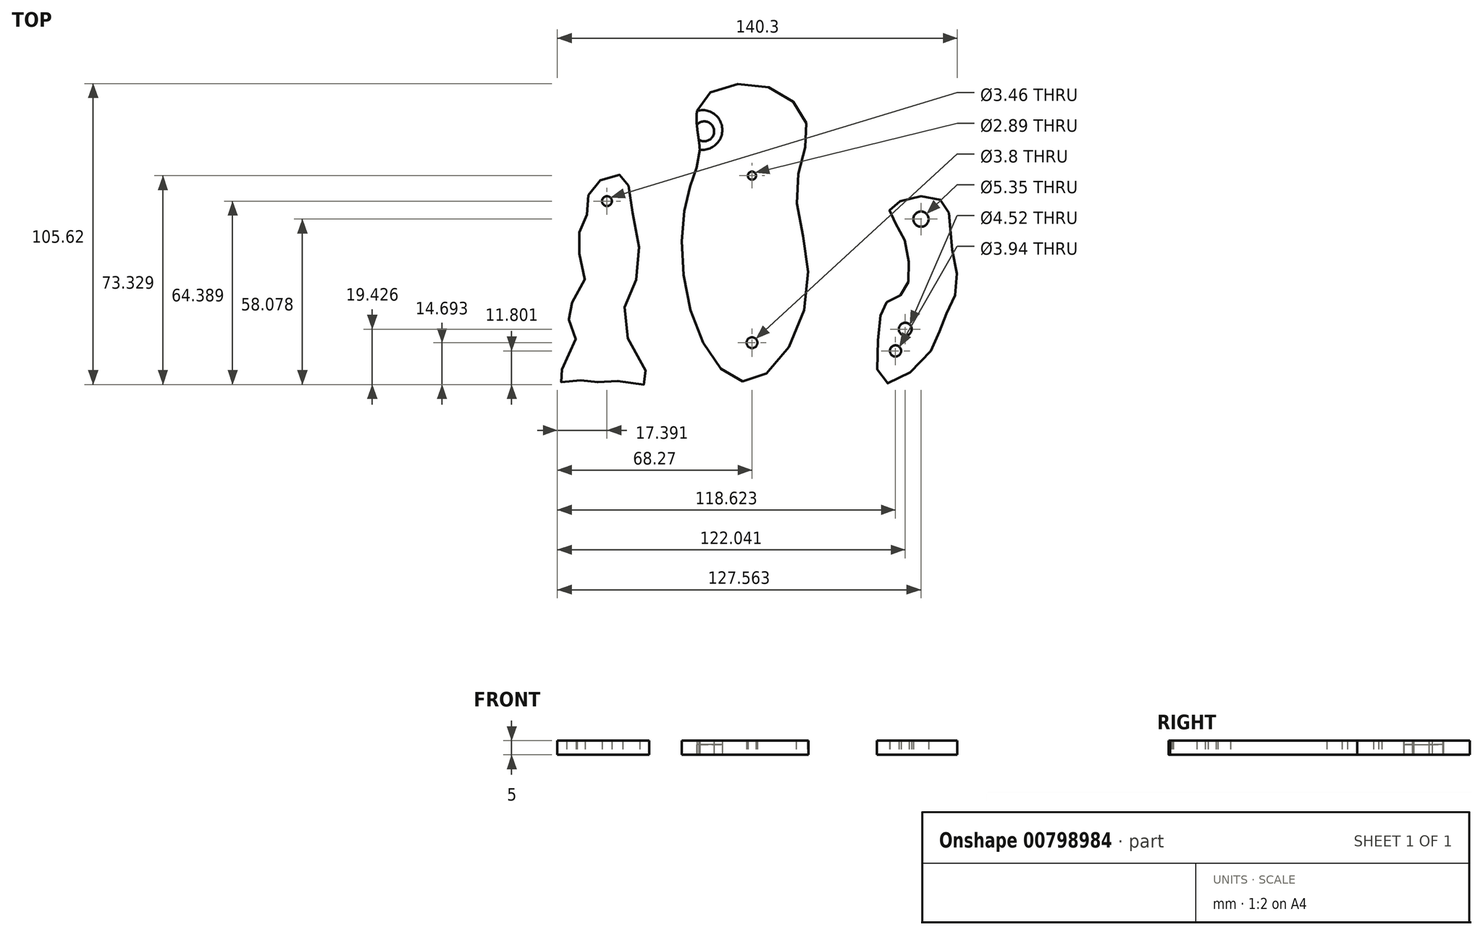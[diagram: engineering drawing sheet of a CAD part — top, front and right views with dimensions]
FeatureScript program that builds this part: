
annotation { "Feature Type Name" : "Feature", "Feature Type Description" : "" }
export const myFeature = defineFeature(function(context is Context, id is Id, definition is map)
    precondition{}
    {
        {
            var Q0;
            Q0=qCreatedBy(makeId("Top.planeOp"),FACE);
            var sketch = newSketch(context, id + "F0", { "sketchPlane" : qUnion([Q0])});
            skFitSpline(sketch, "E0", {"points": [v(-20.9, 21.95) * mm, v(-24.68, 0) * mm, v(-16.62, -36.52) * mm, v(0, -48.9) * mm, v(19.47, -18.26) * mm, v(15.57, 18.83) * mm, v(19.23, 40.4) * mm, v(4.38, 54.6) * mm, v(-18.08, 49.14) * mm, v(-18.34, 32.3) * mm, v(-20.9, 21.95) * mm]});
            skFitSpline(sketch, "E1", {"points": [v(51.93, 14.2) * mm, v(48.25, 10.52) * mm, v(52.2, 3.68) * mm, v(55.09, -9.47) * mm, v(52.98, -18.14) * mm, v(46.93, -21.56) * mm, v(44.57, -30.76) * mm, v(46.15, -49.43) * mm, v(62.18, -39.18) * mm, v(67.18, -27.35) * mm, v(71.91, -16.04) * mm, v(69.81, 0) * mm, v(69.28, 9.47) * mm, v(64.81, 15.25) * mm, v(51.93, 14.2) * mm]});
            skFitSpline(sketch, "E2", {"points": [v(-57.45, 16.3) * mm, v(-51.67, 22.35) * mm, v(-44.83, 22.88) * mm, v(-42.73, 14.46) * mm, v(-39.84, -10.52) * mm, v(-45.1, -29.45) * mm, v(-36.15, -49.43) * mm, v(-47.46, -48.9) * mm, v(-55.61, -49.43) * mm, v(-62.71, -48.64) * mm, v(-68.23, -48.9) * mm, v(-61.66, -32.6) * mm, v(-65.08, -25.24) * mm, v(-58.77, -13.94) * mm, v(-61.4, 0) * mm, v(-58.24, 7.89) * mm, v(-57.45, 16.3) * mm]});
            skArc(sketch, "E3", {"start": v(-18.34, 32.3) * mm, "mid": v(-10.42, 39.66) * mm, "end": v(-19.26, 45.9) * mm});
            skArc(sketch, "E4", {"start": v(-18.68, 35.79) * mm, "mid": v(-13.31, 39.16) * mm, "end": v(-19.36, 41.05) * mm});
            skCircle(sketch, "E5", {"center": v(0, 23.14) * mm, "radius": 1.45 * mm});
            skCircle(sketch, "E6", {"center": v(0, -35.5) * mm, "radius": 1.9 * mm});
            skCircle(sketch, "E7", {"center": v(50.35, -38.39) * mm, "radius": 1.97 * mm});
            skCircle(sketch, "E8", {"center": v(53.77, -30.76) * mm, "radius": 2.26 * mm});
            skCircle(sketch, "E9", {"center": v(59.3, 7.89) * mm, "radius": 2.68 * mm});
            skCircle(sketch, "E10", {"center": v(-50.88, 14.2) * mm, "radius": 1.73 * mm});
            skSolve(sketch);
        }
        {
            var Q0;
            {var subQ0=sQuery(id+"F0.wireOp",EDGE,"E3");Q0=makeQuery(id+"F0.imprint","IMPRINT",FACE,{"disambiguationData":[TD([[makeQuery(id+"F0.imprint","IMPRINT",EDGE,{"derivedFrom":subQ0}),-1.0]])]});}
            var Q1;
            {var subQ0=sQuery(id+"F0.wireOp",EDGE,"E4");Q1=makeQuery(id+"F0.imprint","IMPRINT",FACE,{"disambiguationData":[TD([[makeQuery(id+"F0.imprint","IMPRINT",EDGE,{"derivedFrom":subQ0}),1.0]])]});}
            var Q2;
            Q2=makeQuery(id+"F0.imprint","IMPRINT",FACE,{"disambiguationData":[TD([[makeQuery(id+"F0.imprint","IMPRINT",EDGE,{"derivedFrom":sQuery(id+"F0.wireOp",EDGE,"E1")}),1.0]])]});
            var Q3;
            Q3=makeQuery(id+"F0.imprint","IMPRINT",FACE,{"disambiguationData":[TD([[makeQuery(id+"F0.imprint","IMPRINT",EDGE,{"derivedFrom":sQuery(id+"F0.wireOp",EDGE,"E2")}),-1.0]])]});
            extrude(context, id + "F1", {"entities" : qUnion([Q0, Q1, Q2, Q3]), "depth" : 5 * mm, "offsetDistance" : 25 * mm});
        }
        {
            var Q0;
            {var subQ0=sQuery(id+"F0.wireOp",EDGE,"E3");Q0=makeQuery(id+"F0.imprint","IMPRINT",FACE,{"disambiguationData":[TD([[makeQuery(id+"F0.imprint","IMPRINT",EDGE,{"derivedFrom":subQ0}),1.0]])]});}
            extrude(context, id + "F2", {"entities" : qUnion([Q0]), "depth" : 3.6 * mm, "offsetDistance" : 25 * mm});
        }
    });
